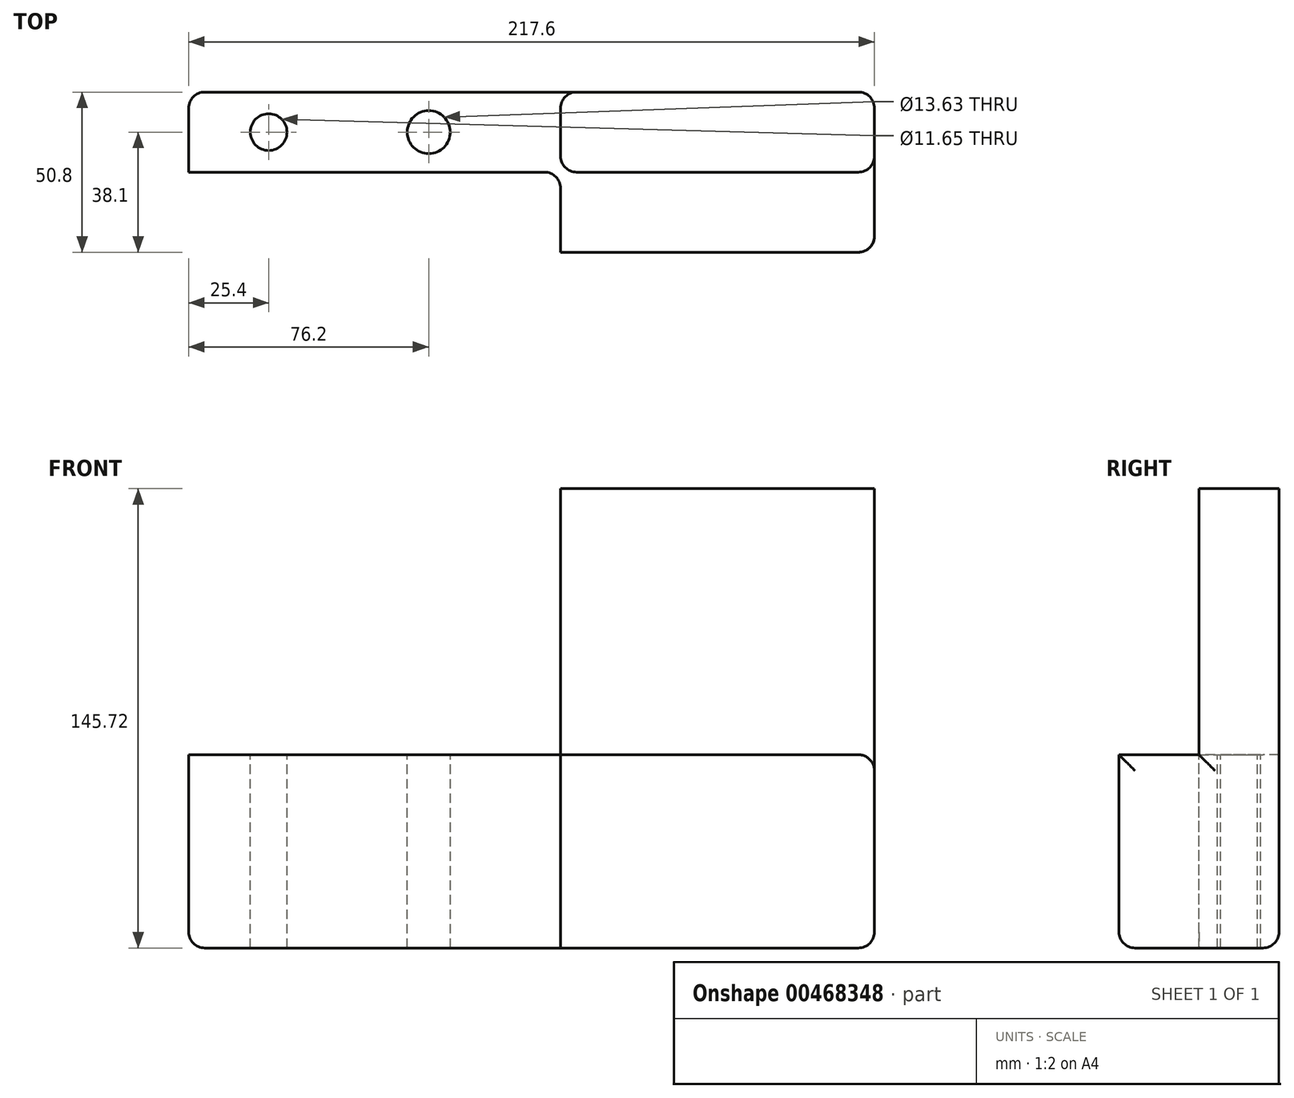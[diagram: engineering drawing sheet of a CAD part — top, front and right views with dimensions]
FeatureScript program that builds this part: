
annotation { "Feature Type Name" : "Feature", "Feature Type Description" : "" }
export const myFeature = defineFeature(function(context is Context, id is Id, definition is map)
    precondition{}
    {
        {
            var Q0;
            Q0=qCreatedBy(makeId("Front.planeOp"),FACE);
            var sketch = newSketch(context, id + "F0", { "sketchPlane" : qUnion([Q0])});
            skLineSegment(sketch, "E0", {"start": v(0, 0) * mm, "end": v(118, 0) * mm});
            skLineSegment(sketch, "E1", {"start": v(118, 0) * mm, "end": v(118, 84.4) * mm});
            skLineSegment(sketch, "E2", {"start": v(118, 84.4) * mm, "end": v(217.6, 84.4) * mm});
            skLineSegment(sketch, "E3", {"start": v(217.6, 84.4) * mm, "end": v(217.6, -61.3) * mm});
            skLineSegment(sketch, "E4", {"start": v(217.6, -61.3) * mm, "end": v(0, -61.3) * mm});
            skLineSegment(sketch, "E5", {"start": v(0, -61.3) * mm, "end": v(0, 0) * mm});
            skSolve(sketch);
        }
        {
            var Q0;
            Q0=makeQuery(id+"F0.imprint","IMPRINT",FACE,{"disambiguationData":[TD([[makeQuery(id+"F0.imprint","IMPRINT",EDGE,{"derivedFrom":sQuery(id+"F0.wireOp",EDGE,"E0")}),-1.0]])]});
            extrude(context, id + "F1", {"entities" : qUnion([Q0]), "depth" : 25.4 * mm});
        }
        {
            var Q0;
            Q0=makeQuery(id+"F1.opExtrude","SWEPT_FACE",FACE,{"disambiguationData":[OSD([sQuery(id+"F0.wireOp",EDGE,"E0")])]});
            var sketch = newSketch(context, id + "F2", { "sketchPlane" : qUnion([Q0])});
            skCircle(sketch, "E6", {"center": v(76.2, -12.7) * mm, "radius": 6.82 * mm});
            skPoint(sketch, "E6.centerSnap0", {"position": v(118, -12.7) * mm});
            skCircle(sketch, "E7", {"center": v(25.4, -12.7) * mm, "radius": 5.82 * mm});
            skSolve(sketch);
        }
        {
            var Q0;
            Q0=makeQuery(id+"F2.imprint","IMPRINT",FACE,{"disambiguationData":[TD([[makeQuery(id+"F2.imprint","IMPRINT",EDGE,{"derivedFrom":sQuery(id+"F2.wireOp",EDGE,"E7")}),1.0]])]});
            var Q1;
            Q1=makeQuery(id+"F2.imprint","IMPRINT",FACE,{"disambiguationData":[TD([[makeQuery(id+"F2.imprint","IMPRINT",EDGE,{"derivedFrom":sQuery(id+"F2.wireOp",EDGE,"E6")}),1.0]])]});
            extrude(context, id + "F3", {"entities" : qUnion([Q0, Q1]), "operationType" : NewBodyOperationType.REMOVE, "oppositeDirection" : true, "depth" : 152.4 * mm});
        }
        {
            var Q0;
            Q0=makeQuery(id+"F1.opExtrude","CAP_FACE",FACE,{"disambiguationData":[OSD([sQuery(id+"F0.wireOp",EDGE,"E0"),sQuery(id+"F0.wireOp",EDGE,"E1"),sQuery(id+"F0.wireOp",EDGE,"E2"),sQuery(id+"F0.wireOp",EDGE,"E3"),sQuery(id+"F0.wireOp",EDGE,"E4"),sQuery(id+"F0.wireOp",EDGE,"E5")])],"isStart":false});
            var sketch = newSketch(context, id + "F4", { "sketchPlane" : qUnion([Q0])});
            skLineSegment(sketch, "E8.bottom", {"start": v(217.6, -61.3) * mm, "end": v(118, -61.3) * mm});
            skLineSegment(sketch, "E8.top", {"start": v(217.6, 0) * mm, "end": v(118, 0) * mm});
            skLineSegment(sketch, "E8.left", {"start": v(217.6, -61.3) * mm, "end": v(217.6, 0) * mm});
            skLineSegment(sketch, "E8.right", {"start": v(118, -61.3) * mm, "end": v(118, 0) * mm});
            skSolve(sketch);
        }
        {
            var Q0;
            Q0=makeQuery(id+"F4.imprint","IMPRINT",FACE,{"disambiguationData":[TD([[makeQuery(id+"F4.imprint","IMPRINT",EDGE,{"derivedFrom":sQuery(id+"F4.wireOp",EDGE,"E8.bottom")}),-1.0]])]});
            extrude(context, id + "F5", {"entities" : qUnion([Q0]), "operationType" : NewBodyOperationType.ADD, "depth" : 25.4 * mm});
        }
        {
            var Q0;
            Q0=makeQuery(id+"F5.opExtrude","CAP_EDGE",EDGE,{"disambiguationData":[OSD([sQuery(id+"F4.wireOp",EDGE,"E8.right")])],"isStart":true});
            fillet(context, id + "F6", {"entities" : qUnion([Q0]), "radius" : 5.08 * mm, "tangentPropagation" : true, "allowEdgeOverflow" : false});
        }
        {
            var Q0;
            Q0=makeQuery(id+"F1.opExtrude","CAP_EDGE",EDGE,{"disambiguationData":[OSD([sQuery(id+"F0.wireOp",EDGE,"E1")])],"isStart":false});
            fillet(context, id + "F7", {"entities" : qUnion([Q0]), "radius" : 5.08 * mm, "tangentPropagation" : true, "allowEdgeOverflow" : false});
        }
        {
            var Q0;
            Q0=makeQuery(id+"F1.opExtrude","CAP_EDGE",EDGE,{"disambiguationData":[OSD([sQuery(id+"F0.wireOp",EDGE,"E3")])],"isStart":false});
            fillet(context, id + "F8", {"entities" : qUnion([Q0]), "radius" : 5.08 * mm, "tangentPropagation" : true, "allowEdgeOverflow" : false});
        }
        {
            var Q0;
            Q0=makeQuery(id+"F5.opExtrude","SWEPT_EDGE",EDGE,{"disambiguationData":[OSD([sQuery(id+"F0.wireOp",EDGE,"E3"),sQuery(id+"F4.wireOp",EDGE,"E8.top"),sQuery(id+"F4.wireOp",EDGE,"E8.left")])]});
            var Q1;
            Q1=makeQuery(id+"F5.opExtrude","CAP_EDGE",EDGE,{"disambiguationData":[OSD([sQuery(id+"F4.wireOp",EDGE,"E8.left")])],"isStart":false});
            fillet(context, id + "F9", {"entities" : qUnion([Q0, Q1]), "radius" : 5.08 * mm, "tangentPropagation" : true, "allowEdgeOverflow" : false});
        }
        {
            var Q0;
            Q0=makeQuery(id+"F5.boolean.opBoolean","MERGE",EDGE,{"derivedFrom":[makeQuery(id+"F1.opExtrude","SWEPT_EDGE",EDGE,{"disambiguationData":[OSD([sQuery(id+"F0.wireOp",EDGE,"E3"),sQuery(id+"F0.wireOp",EDGE,"E4")])]}),makeQuery(id+"F5.opExtrude","SWEPT_EDGE",EDGE,{"disambiguationData":[OSD([sQuery(id+"F4.wireOp",EDGE,"E8.bottom"),sQuery(id+"F4.wireOp",EDGE,"E8.left")])]})]});
            fillet(context, id + "F10", {"entities" : qUnion([Q0]), "radius" : 5.08 * mm, "tangentPropagation" : true, "allowEdgeOverflow" : false});
        }
        {
            var Q0;
            Q0=makeQuery(id+"F1.opExtrude","CAP_EDGE",EDGE,{"disambiguationData":[OSD([sQuery(id+"F0.wireOp",EDGE,"E3")])],"isStart":true});
            fillet(context, id + "F11", {"entities" : qUnion([Q0]), "radius" : 5.08 * mm, "tangentPropagation" : true, "allowEdgeOverflow" : false});
        }
        {
            var Q0;
            Q0=makeQuery(id+"F1.opExtrude","CAP_EDGE",EDGE,{"disambiguationData":[OSD([sQuery(id+"F0.wireOp",EDGE,"E1")])],"isStart":true});
            fillet(context, id + "F12", {"entities" : qUnion([Q0]), "radius" : 5.08 * mm, "tangentPropagation" : true, "allowEdgeOverflow" : false});
        }
        {
            var Q0;
            Q0=makeQuery(id+"F1.opExtrude","CAP_EDGE",EDGE,{"disambiguationData":[OSD([sQuery(id+"F0.wireOp",EDGE,"E5")])],"isStart":true});
            fillet(context, id + "F13", {"entities" : qUnion([Q0]), "radius" : 5.08 * mm, "tangentPropagation" : true, "allowEdgeOverflow" : false});
        }
    });
